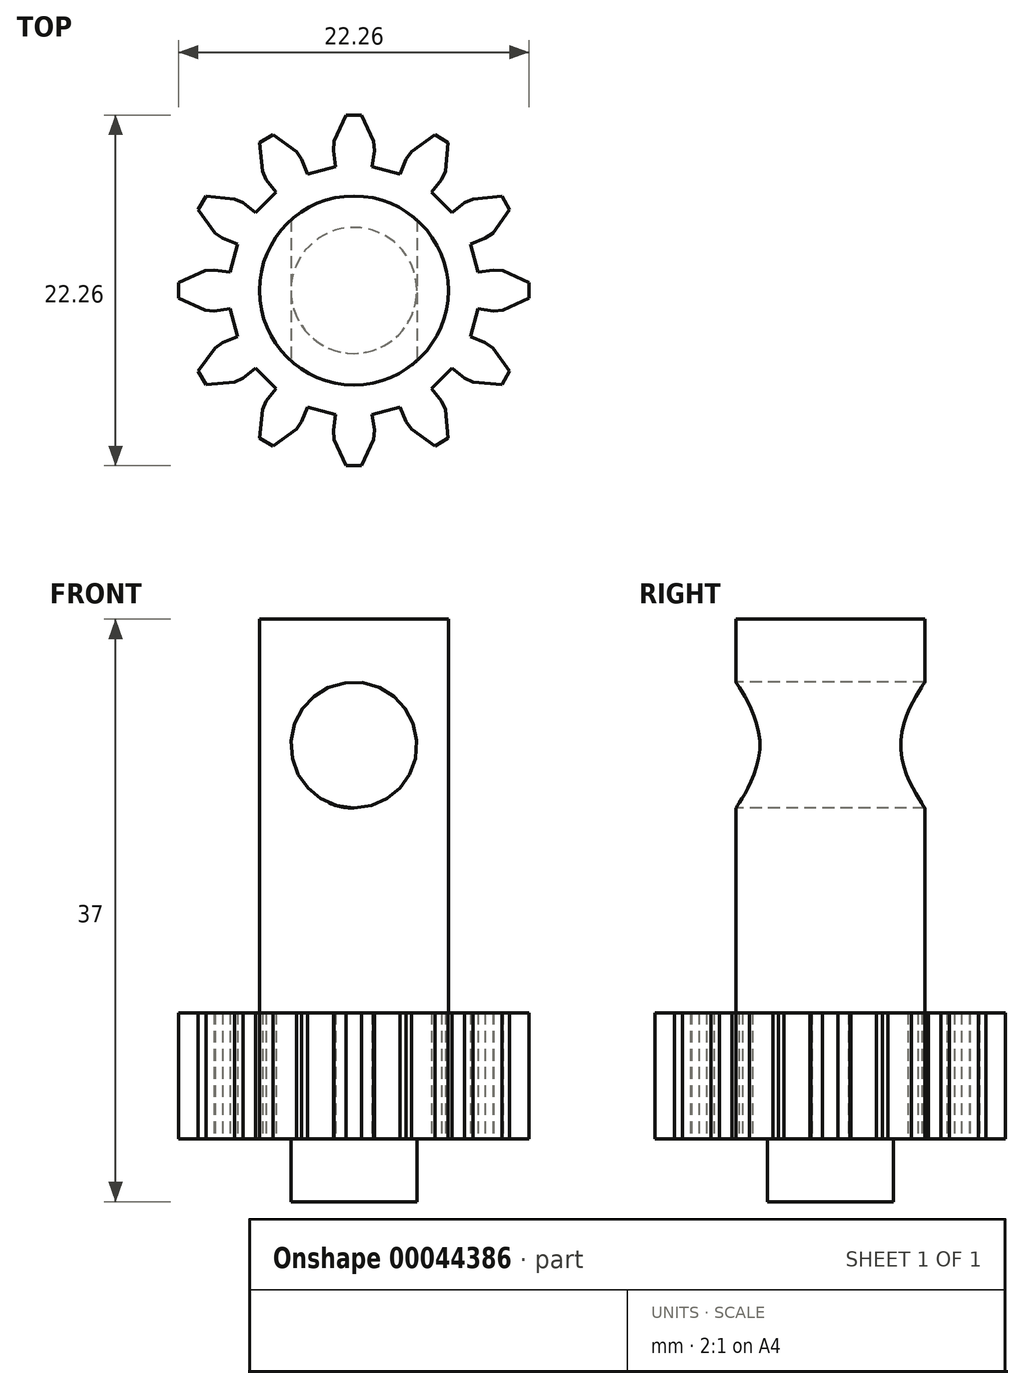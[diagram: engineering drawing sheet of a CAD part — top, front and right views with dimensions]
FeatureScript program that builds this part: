
annotation { "Feature Type Name" : "Feature", "Feature Type Description" : "" }
export const myFeature = defineFeature(function(context is Context, id is Id, definition is map)
    precondition{}
    {
        {
            var Q0;
            Q0=qCreatedBy(makeId("Top.planeOp"),FACE);
            var sketch = newSketch(context, id + "F0", { "sketchPlane" : qUnion([Q0])});
            skLineSegment(sketch, "E0", {"start": v(7.87, 1.16) * mm, "end": v(8.88, 1.3) * mm});
            skLineSegment(sketch, "E1", {"start": v(8.88, 1.3) * mm, "end": v(9.47, 1.25) * mm});
            skLineSegment(sketch, "E2", {"start": v(9.47, 1.25) * mm, "end": v(11.13, 0.5) * mm});
            skLineSegment(sketch, "E3", {"start": v(11.13, 0.5) * mm, "end": v(11.13, -0.5) * mm});
            skLineSegment(sketch, "E4", {"start": v(11.13, -0.5) * mm, "end": v(9.47, -1.25) * mm});
            skLineSegment(sketch, "E5", {"start": v(9.47, -1.25) * mm, "end": v(8.88, -1.3) * mm});
            skLineSegment(sketch, "E6", {"start": v(8.88, -1.3) * mm, "end": v(7.87, -1.16) * mm});
            skLineSegment(sketch, "E7", {"start": v(7.87, -1.16) * mm, "end": v(7.4, -2.94) * mm});
            skLineSegment(sketch, "E8", {"start": v(7.4, -2.94) * mm, "end": v(8.34, -3.31) * mm});
            skLineSegment(sketch, "E9", {"start": v(8.34, -3.31) * mm, "end": v(8.82, -3.65) * mm});
            skLineSegment(sketch, "E10", {"start": v(8.82, -3.65) * mm, "end": v(9.89, -5.14) * mm});
            skLineSegment(sketch, "E11", {"start": v(9.89, -5.14) * mm, "end": v(9.4, -6) * mm});
            skLineSegment(sketch, "E12", {"start": v(9.4, -6) * mm, "end": v(7.58, -5.81) * mm});
            skLineSegment(sketch, "E13", {"start": v(7.58, -5.81) * mm, "end": v(7.04, -5.57) * mm});
            skLineSegment(sketch, "E14", {"start": v(7.04, -5.57) * mm, "end": v(6.24, -4.94) * mm});
            skLineSegment(sketch, "E15", {"start": v(6.24, -4.94) * mm, "end": v(4.94, -6.24) * mm});
            skLineSegment(sketch, "E16", {"start": v(4.94, -6.24) * mm, "end": v(5.57, -7.04) * mm});
            skLineSegment(sketch, "E17", {"start": v(5.57, -7.04) * mm, "end": v(5.81, -7.58) * mm});
            skLineSegment(sketch, "E18", {"start": v(5.81, -7.58) * mm, "end": v(6, -9.4) * mm});
            skLineSegment(sketch, "E19", {"start": v(6, -9.4) * mm, "end": v(5.14, -9.89) * mm});
            skLineSegment(sketch, "E20", {"start": v(5.14, -9.89) * mm, "end": v(3.65, -8.82) * mm});
            skLineSegment(sketch, "E21", {"start": v(3.65, -8.82) * mm, "end": v(3.31, -8.34) * mm});
            skLineSegment(sketch, "E22", {"start": v(3.31, -8.34) * mm, "end": v(2.94, -7.4) * mm});
            skLineSegment(sketch, "E23", {"start": v(2.94, -7.4) * mm, "end": v(1.16, -7.87) * mm});
            skLineSegment(sketch, "E24", {"start": v(1.16, -7.87) * mm, "end": v(1.3, -8.88) * mm});
            skLineSegment(sketch, "E25", {"start": v(1.3, -8.88) * mm, "end": v(1.25, -9.47) * mm});
            skLineSegment(sketch, "E26", {"start": v(1.25, -9.47) * mm, "end": v(0.5, -11.13) * mm});
            skLineSegment(sketch, "E27", {"start": v(0.5, -11.13) * mm, "end": v(-0.5, -11.13) * mm});
            skLineSegment(sketch, "E28", {"start": v(-0.5, -11.13) * mm, "end": v(-1.25, -9.47) * mm});
            skLineSegment(sketch, "E29", {"start": v(-1.25, -9.47) * mm, "end": v(-1.3, -8.88) * mm});
            skLineSegment(sketch, "E30", {"start": v(-1.3, -8.88) * mm, "end": v(-1.16, -7.87) * mm});
            skLineSegment(sketch, "E31", {"start": v(-1.16, -7.87) * mm, "end": v(-2.94, -7.4) * mm});
            skLineSegment(sketch, "E32", {"start": v(-2.94, -7.4) * mm, "end": v(-3.31, -8.34) * mm});
            skLineSegment(sketch, "E33", {"start": v(-3.31, -8.34) * mm, "end": v(-3.65, -8.82) * mm});
            skLineSegment(sketch, "E34", {"start": v(-3.65, -8.82) * mm, "end": v(-5.14, -9.89) * mm});
            skLineSegment(sketch, "E35", {"start": v(-5.14, -9.89) * mm, "end": v(-6, -9.4) * mm});
            skLineSegment(sketch, "E36", {"start": v(-6, -9.4) * mm, "end": v(-5.81, -7.58) * mm});
            skLineSegment(sketch, "E37", {"start": v(-5.81, -7.58) * mm, "end": v(-5.57, -7.04) * mm});
            skLineSegment(sketch, "E38", {"start": v(-5.57, -7.04) * mm, "end": v(-4.94, -6.24) * mm});
            skLineSegment(sketch, "E39", {"start": v(-4.94, -6.24) * mm, "end": v(-6.24, -4.94) * mm});
            skLineSegment(sketch, "E40", {"start": v(-6.24, -4.94) * mm, "end": v(-7.04, -5.57) * mm});
            skLineSegment(sketch, "E41", {"start": v(-7.04, -5.57) * mm, "end": v(-7.58, -5.81) * mm});
            skLineSegment(sketch, "E42", {"start": v(-7.58, -5.81) * mm, "end": v(-9.4, -6) * mm});
            skLineSegment(sketch, "E43", {"start": v(-9.4, -6) * mm, "end": v(-9.89, -5.14) * mm});
            skLineSegment(sketch, "E44", {"start": v(-9.89, -5.14) * mm, "end": v(-8.82, -3.65) * mm});
            skLineSegment(sketch, "E45", {"start": v(-8.82, -3.65) * mm, "end": v(-8.34, -3.31) * mm});
            skLineSegment(sketch, "E46", {"start": v(-8.34, -3.31) * mm, "end": v(-7.4, -2.94) * mm});
            skLineSegment(sketch, "E47", {"start": v(-7.4, -2.94) * mm, "end": v(-7.87, -1.16) * mm});
            skLineSegment(sketch, "E48", {"start": v(-7.87, -1.16) * mm, "end": v(-8.88, -1.3) * mm});
            skLineSegment(sketch, "E49", {"start": v(-8.88, -1.3) * mm, "end": v(-9.47, -1.25) * mm});
            skLineSegment(sketch, "E50", {"start": v(-9.47, -1.25) * mm, "end": v(-11.13, -0.5) * mm});
            skLineSegment(sketch, "E51", {"start": v(-11.13, -0.5) * mm, "end": v(-11.13, 0.5) * mm});
            skLineSegment(sketch, "E52", {"start": v(-11.13, 0.5) * mm, "end": v(-9.47, 1.25) * mm});
            skLineSegment(sketch, "E53", {"start": v(-9.47, 1.25) * mm, "end": v(-8.88, 1.3) * mm});
            skLineSegment(sketch, "E54", {"start": v(-8.88, 1.3) * mm, "end": v(-7.87, 1.16) * mm});
            skLineSegment(sketch, "E55", {"start": v(-7.87, 1.16) * mm, "end": v(-7.4, 2.94) * mm});
            skLineSegment(sketch, "E56", {"start": v(-7.4, 2.94) * mm, "end": v(-8.34, 3.31) * mm});
            skLineSegment(sketch, "E57", {"start": v(-8.34, 3.31) * mm, "end": v(-8.82, 3.65) * mm});
            skLineSegment(sketch, "E58", {"start": v(-8.82, 3.65) * mm, "end": v(-9.89, 5.14) * mm});
            skLineSegment(sketch, "E59", {"start": v(-9.89, 5.14) * mm, "end": v(-9.4, 6) * mm});
            skLineSegment(sketch, "E60", {"start": v(-9.4, 6) * mm, "end": v(-7.58, 5.81) * mm});
            skLineSegment(sketch, "E61", {"start": v(-7.58, 5.81) * mm, "end": v(-7.04, 5.57) * mm});
            skLineSegment(sketch, "E62", {"start": v(-7.04, 5.57) * mm, "end": v(-6.24, 4.94) * mm});
            skLineSegment(sketch, "E63", {"start": v(-6.24, 4.94) * mm, "end": v(-4.94, 6.24) * mm});
            skLineSegment(sketch, "E64", {"start": v(-4.94, 6.24) * mm, "end": v(-5.57, 7.04) * mm});
            skLineSegment(sketch, "E65", {"start": v(-5.57, 7.04) * mm, "end": v(-5.81, 7.58) * mm});
            skLineSegment(sketch, "E66", {"start": v(-5.81, 7.58) * mm, "end": v(-6, 9.4) * mm});
            skLineSegment(sketch, "E67", {"start": v(-6, 9.4) * mm, "end": v(-5.14, 9.89) * mm});
            skLineSegment(sketch, "E68", {"start": v(-5.14, 9.89) * mm, "end": v(-3.65, 8.82) * mm});
            skLineSegment(sketch, "E69", {"start": v(-3.65, 8.82) * mm, "end": v(-3.31, 8.34) * mm});
            skLineSegment(sketch, "E70", {"start": v(-3.31, 8.34) * mm, "end": v(-2.94, 7.4) * mm});
            skLineSegment(sketch, "E71", {"start": v(-2.94, 7.4) * mm, "end": v(-1.16, 7.87) * mm});
            skLineSegment(sketch, "E72", {"start": v(-1.16, 7.87) * mm, "end": v(-1.3, 8.88) * mm});
            skLineSegment(sketch, "E73", {"start": v(-1.3, 8.88) * mm, "end": v(-1.25, 9.47) * mm});
            skLineSegment(sketch, "E74", {"start": v(-1.25, 9.47) * mm, "end": v(-0.5, 11.13) * mm});
            skLineSegment(sketch, "E75", {"start": v(-0.5, 11.13) * mm, "end": v(0.5, 11.13) * mm});
            skLineSegment(sketch, "E76", {"start": v(0.5, 11.13) * mm, "end": v(1.25, 9.47) * mm});
            skLineSegment(sketch, "E77", {"start": v(1.25, 9.47) * mm, "end": v(1.3, 8.88) * mm});
            skLineSegment(sketch, "E78", {"start": v(1.3, 8.88) * mm, "end": v(1.16, 7.87) * mm});
            skLineSegment(sketch, "E79", {"start": v(1.16, 7.87) * mm, "end": v(2.94, 7.4) * mm});
            skLineSegment(sketch, "E80", {"start": v(2.94, 7.4) * mm, "end": v(3.31, 8.34) * mm});
            skLineSegment(sketch, "E81", {"start": v(3.31, 8.34) * mm, "end": v(3.65, 8.82) * mm});
            skLineSegment(sketch, "E82", {"start": v(3.65, 8.82) * mm, "end": v(5.14, 9.89) * mm});
            skLineSegment(sketch, "E83", {"start": v(5.14, 9.89) * mm, "end": v(6, 9.4) * mm});
            skLineSegment(sketch, "E84", {"start": v(6, 9.4) * mm, "end": v(5.81, 7.58) * mm});
            skLineSegment(sketch, "E85", {"start": v(5.81, 7.58) * mm, "end": v(5.57, 7.04) * mm});
            skLineSegment(sketch, "E86", {"start": v(5.57, 7.04) * mm, "end": v(4.94, 6.24) * mm});
            skLineSegment(sketch, "E87", {"start": v(4.94, 6.24) * mm, "end": v(6.24, 4.94) * mm});
            skLineSegment(sketch, "E88", {"start": v(6.24, 4.94) * mm, "end": v(7.04, 5.57) * mm});
            skLineSegment(sketch, "E89", {"start": v(7.04, 5.57) * mm, "end": v(7.58, 5.81) * mm});
            skLineSegment(sketch, "E90", {"start": v(7.58, 5.81) * mm, "end": v(9.4, 6) * mm});
            skLineSegment(sketch, "E91", {"start": v(9.4, 6) * mm, "end": v(9.89, 5.14) * mm});
            skLineSegment(sketch, "E92", {"start": v(9.89, 5.14) * mm, "end": v(8.82, 3.65) * mm});
            skLineSegment(sketch, "E93", {"start": v(8.82, 3.65) * mm, "end": v(8.34, 3.31) * mm});
            skLineSegment(sketch, "E94", {"start": v(8.34, 3.31) * mm, "end": v(7.4, 2.94) * mm});
            skLineSegment(sketch, "E95", {"start": v(7.4, 2.94) * mm, "end": v(7.87, 1.16) * mm});
            skSolve(sketch);
        }
        {
            var Q0;
            Q0=makeQuery(id+"F0.imprint","IMPRINT",FACE,{"disambiguationData":[TD([[makeQuery(id+"F0.imprint","IMPRINT",EDGE,{"derivedFrom":sQuery(id+"F0.wireOp",EDGE,"E0")}),-1.0]])]});
            extrude(context, id + "F1", {"entities" : qUnion([Q0]), "depth" : 8 * mm});
        }
        {
            var Q0;
            Q0=makeQuery(id+"F1.opExtrude","CAP_FACE",FACE,{"disambiguationData":[OSD([sQuery(id+"F0.wireOp",EDGE,"E0"),sQuery(id+"F0.wireOp",EDGE,"E1"),sQuery(id+"F0.wireOp",EDGE,"E2"),sQuery(id+"F0.wireOp",EDGE,"E3"),sQuery(id+"F0.wireOp",EDGE,"E4"),sQuery(id+"F0.wireOp",EDGE,"E5"),sQuery(id+"F0.wireOp",EDGE,"E6"),sQuery(id+"F0.wireOp",EDGE,"E7"),sQuery(id+"F0.wireOp",EDGE,"E8"),sQuery(id+"F0.wireOp",EDGE,"E9"),sQuery(id+"F0.wireOp",EDGE,"E10"),sQuery(id+"F0.wireOp",EDGE,"E11"),sQuery(id+"F0.wireOp",EDGE,"E12"),sQuery(id+"F0.wireOp",EDGE,"E13"),sQuery(id+"F0.wireOp",EDGE,"E14"),sQuery(id+"F0.wireOp",EDGE,"E15"),sQuery(id+"F0.wireOp",EDGE,"E16"),sQuery(id+"F0.wireOp",EDGE,"E17"),sQuery(id+"F0.wireOp",EDGE,"E18"),sQuery(id+"F0.wireOp",EDGE,"E19"),sQuery(id+"F0.wireOp",EDGE,"E20"),sQuery(id+"F0.wireOp",EDGE,"E21"),sQuery(id+"F0.wireOp",EDGE,"E22"),sQuery(id+"F0.wireOp",EDGE,"E23"),sQuery(id+"F0.wireOp",EDGE,"E24"),sQuery(id+"F0.wireOp",EDGE,"E25"),sQuery(id+"F0.wireOp",EDGE,"E26"),sQuery(id+"F0.wireOp",EDGE,"E27"),sQuery(id+"F0.wireOp",EDGE,"E28"),sQuery(id+"F0.wireOp",EDGE,"E29"),sQuery(id+"F0.wireOp",EDGE,"E30"),sQuery(id+"F0.wireOp",EDGE,"E31"),sQuery(id+"F0.wireOp",EDGE,"E32"),sQuery(id+"F0.wireOp",EDGE,"E33"),sQuery(id+"F0.wireOp",EDGE,"E34"),sQuery(id+"F0.wireOp",EDGE,"E35"),sQuery(id+"F0.wireOp",EDGE,"E36"),sQuery(id+"F0.wireOp",EDGE,"E37"),sQuery(id+"F0.wireOp",EDGE,"E38"),sQuery(id+"F0.wireOp",EDGE,"E39"),sQuery(id+"F0.wireOp",EDGE,"E40"),sQuery(id+"F0.wireOp",EDGE,"E41"),sQuery(id+"F0.wireOp",EDGE,"E42"),sQuery(id+"F0.wireOp",EDGE,"E43"),sQuery(id+"F0.wireOp",EDGE,"E44"),sQuery(id+"F0.wireOp",EDGE,"E45"),sQuery(id+"F0.wireOp",EDGE,"E46"),sQuery(id+"F0.wireOp",EDGE,"E47"),sQuery(id+"F0.wireOp",EDGE,"E48"),sQuery(id+"F0.wireOp",EDGE,"E49"),sQuery(id+"F0.wireOp",EDGE,"E50"),sQuery(id+"F0.wireOp",EDGE,"E51"),sQuery(id+"F0.wireOp",EDGE,"E52"),sQuery(id+"F0.wireOp",EDGE,"E53"),sQuery(id+"F0.wireOp",EDGE,"E54"),sQuery(id+"F0.wireOp",EDGE,"E55"),sQuery(id+"F0.wireOp",EDGE,"E56"),sQuery(id+"F0.wireOp",EDGE,"E57"),sQuery(id+"F0.wireOp",EDGE,"E58"),sQuery(id+"F0.wireOp",EDGE,"E59"),sQuery(id+"F0.wireOp",EDGE,"E60"),sQuery(id+"F0.wireOp",EDGE,"E61"),sQuery(id+"F0.wireOp",EDGE,"E62"),sQuery(id+"F0.wireOp",EDGE,"E63"),sQuery(id+"F0.wireOp",EDGE,"E64"),sQuery(id+"F0.wireOp",EDGE,"E65"),sQuery(id+"F0.wireOp",EDGE,"E66"),sQuery(id+"F0.wireOp",EDGE,"E67"),sQuery(id+"F0.wireOp",EDGE,"E68"),sQuery(id+"F0.wireOp",EDGE,"E69"),sQuery(id+"F0.wireOp",EDGE,"E70"),sQuery(id+"F0.wireOp",EDGE,"E71"),sQuery(id+"F0.wireOp",EDGE,"E72"),sQuery(id+"F0.wireOp",EDGE,"E73"),sQuery(id+"F0.wireOp",EDGE,"E74"),sQuery(id+"F0.wireOp",EDGE,"E75"),sQuery(id+"F0.wireOp",EDGE,"E76"),sQuery(id+"F0.wireOp",EDGE,"E77"),sQuery(id+"F0.wireOp",EDGE,"E78"),sQuery(id+"F0.wireOp",EDGE,"E79"),sQuery(id+"F0.wireOp",EDGE,"E80"),sQuery(id+"F0.wireOp",EDGE,"E81"),sQuery(id+"F0.wireOp",EDGE,"E82"),sQuery(id+"F0.wireOp",EDGE,"E83"),sQuery(id+"F0.wireOp",EDGE,"E84"),sQuery(id+"F0.wireOp",EDGE,"E85"),sQuery(id+"F0.wireOp",EDGE,"E86"),sQuery(id+"F0.wireOp",EDGE,"E87"),sQuery(id+"F0.wireOp",EDGE,"E88"),sQuery(id+"F0.wireOp",EDGE,"E89"),sQuery(id+"F0.wireOp",EDGE,"E90"),sQuery(id+"F0.wireOp",EDGE,"E91"),sQuery(id+"F0.wireOp",EDGE,"E92"),sQuery(id+"F0.wireOp",EDGE,"E93"),sQuery(id+"F0.wireOp",EDGE,"E94"),sQuery(id+"F0.wireOp",EDGE,"E95")])],"isStart":false});
            var sketch = newSketch(context, id + "F2", { "sketchPlane" : qUnion([Q0])});
            skCircle(sketch, "E96", {"center": v(0, 0) * mm, "radius": 6 * mm});
            skSolve(sketch);
        }
        {
            var Q0;
            Q0=makeQuery(id+"F2.imprint","IMPRINT",FACE,{"disambiguationData":[TD([[makeQuery(id+"F2.imprint","IMPRINT",EDGE,{"derivedFrom":sQuery(id+"F2.wireOp",EDGE,"E96")}),1.0]])]});
            extrude(context, id + "F3", {"entities" : qUnion([Q0]), "operationType" : NewBodyOperationType.ADD, "depth" : 25 * mm});
        }
        {
            var Q0;
            Q0=makeQuery(id+"F1.opExtrude","CAP_FACE",FACE,{"disambiguationData":[OSD([sQuery(id+"F0.wireOp",EDGE,"E0"),sQuery(id+"F0.wireOp",EDGE,"E1"),sQuery(id+"F0.wireOp",EDGE,"E2"),sQuery(id+"F0.wireOp",EDGE,"E3"),sQuery(id+"F0.wireOp",EDGE,"E4"),sQuery(id+"F0.wireOp",EDGE,"E5"),sQuery(id+"F0.wireOp",EDGE,"E6"),sQuery(id+"F0.wireOp",EDGE,"E7"),sQuery(id+"F0.wireOp",EDGE,"E8"),sQuery(id+"F0.wireOp",EDGE,"E9"),sQuery(id+"F0.wireOp",EDGE,"E10"),sQuery(id+"F0.wireOp",EDGE,"E11"),sQuery(id+"F0.wireOp",EDGE,"E12"),sQuery(id+"F0.wireOp",EDGE,"E13"),sQuery(id+"F0.wireOp",EDGE,"E14"),sQuery(id+"F0.wireOp",EDGE,"E15"),sQuery(id+"F0.wireOp",EDGE,"E16"),sQuery(id+"F0.wireOp",EDGE,"E17"),sQuery(id+"F0.wireOp",EDGE,"E18"),sQuery(id+"F0.wireOp",EDGE,"E19"),sQuery(id+"F0.wireOp",EDGE,"E20"),sQuery(id+"F0.wireOp",EDGE,"E21"),sQuery(id+"F0.wireOp",EDGE,"E22"),sQuery(id+"F0.wireOp",EDGE,"E23"),sQuery(id+"F0.wireOp",EDGE,"E24"),sQuery(id+"F0.wireOp",EDGE,"E25"),sQuery(id+"F0.wireOp",EDGE,"E26"),sQuery(id+"F0.wireOp",EDGE,"E27"),sQuery(id+"F0.wireOp",EDGE,"E28"),sQuery(id+"F0.wireOp",EDGE,"E29"),sQuery(id+"F0.wireOp",EDGE,"E30"),sQuery(id+"F0.wireOp",EDGE,"E31"),sQuery(id+"F0.wireOp",EDGE,"E32"),sQuery(id+"F0.wireOp",EDGE,"E33"),sQuery(id+"F0.wireOp",EDGE,"E34"),sQuery(id+"F0.wireOp",EDGE,"E35"),sQuery(id+"F0.wireOp",EDGE,"E36"),sQuery(id+"F0.wireOp",EDGE,"E37"),sQuery(id+"F0.wireOp",EDGE,"E38"),sQuery(id+"F0.wireOp",EDGE,"E39"),sQuery(id+"F0.wireOp",EDGE,"E40"),sQuery(id+"F0.wireOp",EDGE,"E41"),sQuery(id+"F0.wireOp",EDGE,"E42"),sQuery(id+"F0.wireOp",EDGE,"E43"),sQuery(id+"F0.wireOp",EDGE,"E44"),sQuery(id+"F0.wireOp",EDGE,"E45"),sQuery(id+"F0.wireOp",EDGE,"E46"),sQuery(id+"F0.wireOp",EDGE,"E47"),sQuery(id+"F0.wireOp",EDGE,"E48"),sQuery(id+"F0.wireOp",EDGE,"E49"),sQuery(id+"F0.wireOp",EDGE,"E50"),sQuery(id+"F0.wireOp",EDGE,"E51"),sQuery(id+"F0.wireOp",EDGE,"E52"),sQuery(id+"F0.wireOp",EDGE,"E53"),sQuery(id+"F0.wireOp",EDGE,"E54"),sQuery(id+"F0.wireOp",EDGE,"E55"),sQuery(id+"F0.wireOp",EDGE,"E56"),sQuery(id+"F0.wireOp",EDGE,"E57"),sQuery(id+"F0.wireOp",EDGE,"E58"),sQuery(id+"F0.wireOp",EDGE,"E59"),sQuery(id+"F0.wireOp",EDGE,"E60"),sQuery(id+"F0.wireOp",EDGE,"E61"),sQuery(id+"F0.wireOp",EDGE,"E62"),sQuery(id+"F0.wireOp",EDGE,"E63"),sQuery(id+"F0.wireOp",EDGE,"E64"),sQuery(id+"F0.wireOp",EDGE,"E65"),sQuery(id+"F0.wireOp",EDGE,"E66"),sQuery(id+"F0.wireOp",EDGE,"E67"),sQuery(id+"F0.wireOp",EDGE,"E68"),sQuery(id+"F0.wireOp",EDGE,"E69"),sQuery(id+"F0.wireOp",EDGE,"E70"),sQuery(id+"F0.wireOp",EDGE,"E71"),sQuery(id+"F0.wireOp",EDGE,"E72"),sQuery(id+"F0.wireOp",EDGE,"E73"),sQuery(id+"F0.wireOp",EDGE,"E74"),sQuery(id+"F0.wireOp",EDGE,"E75"),sQuery(id+"F0.wireOp",EDGE,"E76"),sQuery(id+"F0.wireOp",EDGE,"E77"),sQuery(id+"F0.wireOp",EDGE,"E78"),sQuery(id+"F0.wireOp",EDGE,"E79"),sQuery(id+"F0.wireOp",EDGE,"E80"),sQuery(id+"F0.wireOp",EDGE,"E81"),sQuery(id+"F0.wireOp",EDGE,"E82"),sQuery(id+"F0.wireOp",EDGE,"E83"),sQuery(id+"F0.wireOp",EDGE,"E84"),sQuery(id+"F0.wireOp",EDGE,"E85"),sQuery(id+"F0.wireOp",EDGE,"E86"),sQuery(id+"F0.wireOp",EDGE,"E87"),sQuery(id+"F0.wireOp",EDGE,"E88"),sQuery(id+"F0.wireOp",EDGE,"E89"),sQuery(id+"F0.wireOp",EDGE,"E90"),sQuery(id+"F0.wireOp",EDGE,"E91"),sQuery(id+"F0.wireOp",EDGE,"E92"),sQuery(id+"F0.wireOp",EDGE,"E93"),sQuery(id+"F0.wireOp",EDGE,"E94"),sQuery(id+"F0.wireOp",EDGE,"E95")])],"isStart":true});
            var sketch = newSketch(context, id + "F4", { "sketchPlane" : qUnion([Q0])});
            skCircle(sketch, "E97", {"center": v(0, 0) * mm, "radius": 4 * mm});
            skSolve(sketch);
        }
        {
            var Q0;
            Q0=makeQuery(id+"F4.imprint","IMPRINT",FACE,{"disambiguationData":[TD([[makeQuery(id+"F4.imprint","IMPRINT",EDGE,{"derivedFrom":sQuery(id+"F4.wireOp",EDGE,"E97")}),1.0]])]});
            extrude(context, id + "F5", {"entities" : qUnion([Q0]), "operationType" : NewBodyOperationType.ADD, "depth" : 4 * mm});
        }
        {
            var Q0;
            Q0=qCreatedBy(makeId("Front.planeOp"),FACE);
            var sketch = newSketch(context, id + "F6", { "sketchPlane" : qUnion([Q0])});
            skCircle(sketch, "E98", {"center": v(0, 25) * mm, "radius": 4 * mm});
            skSolve(sketch);
        }
        {
            var Q0;
            Q0 = qSketchRegion(id + "F6", true);
            extrude(context, id + "F7", {"entities" : qUnion([Q0]), "operationType" : NewBodyOperationType.REMOVE, "endBound" : BoundingType.SYMMETRIC, "oppositeDirection" : true, "depth" : 12 * mm});
        }
    });
